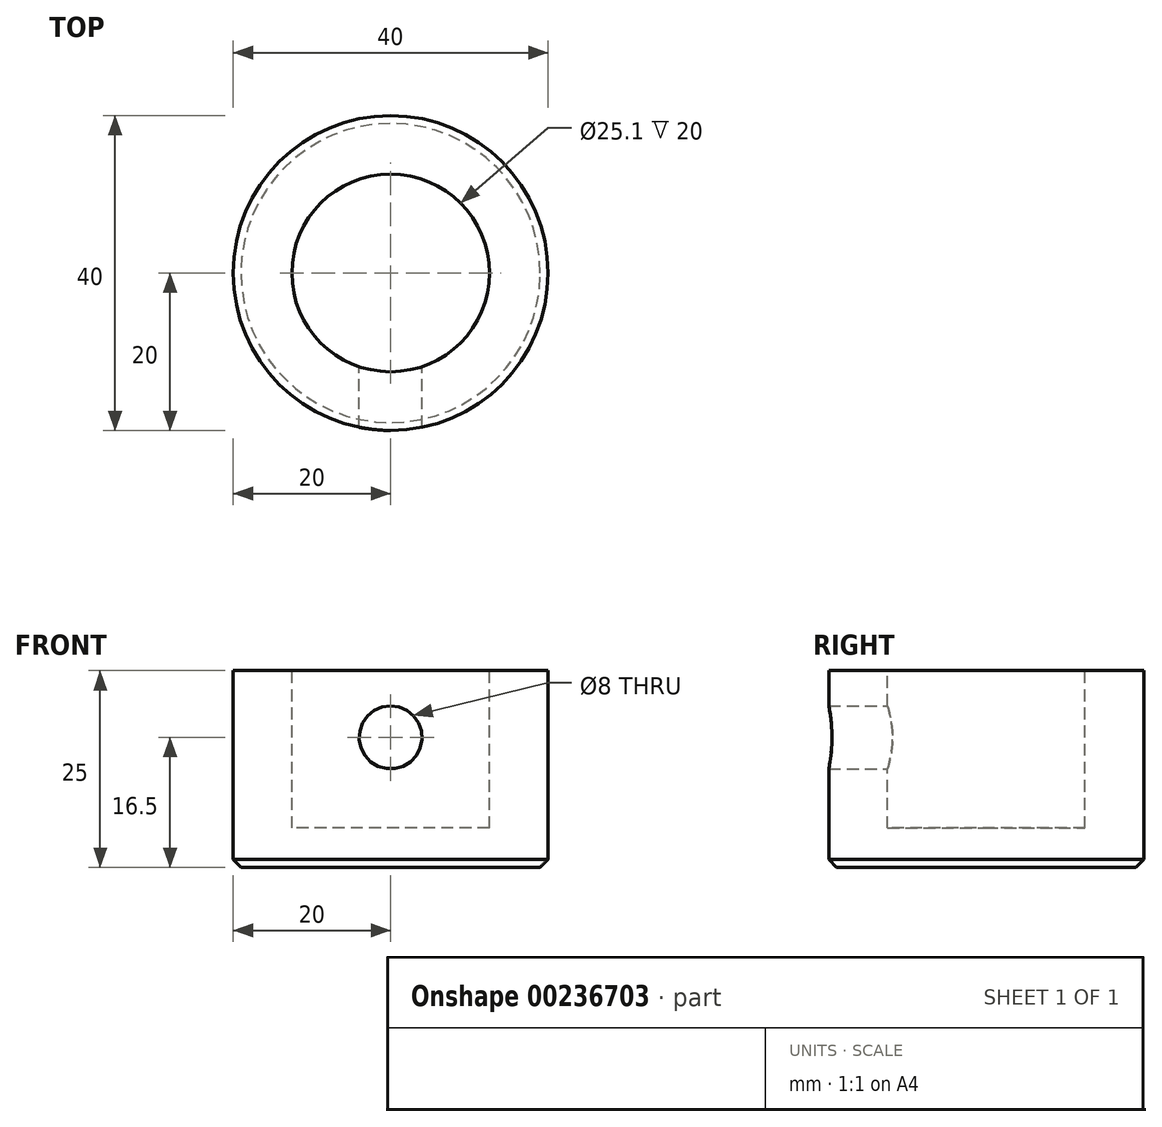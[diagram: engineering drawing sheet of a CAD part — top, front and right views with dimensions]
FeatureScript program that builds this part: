
annotation { "Feature Type Name" : "Feature", "Feature Type Description" : "" }
export const myFeature = defineFeature(function(context is Context, id is Id, definition is map)
    precondition{}
    {
        {
            var Q0;
            Q0=qCreatedBy(makeId("Top.planeOp"),FACE);
            var sketch = newSketch(context, id + "F0", { "sketchPlane" : qUnion([Q0])});
            skCircle(sketch, "E0", {"center": v(0, 0) * mm, "radius": 20 * mm});
            skSolve(sketch);
        }
        {
            var Q0;
            Q0=makeQuery(id+"F0.imprint","IMPRINT",FACE,{"disambiguationData":[TD([[makeQuery(id+"F0.imprint","IMPRINT",EDGE,{"derivedFrom":sQuery(id+"F0.wireOp",EDGE,"E0")}),1.0]])]});
            extrude(context, id + "F1", {"entities" : qUnion([Q0]), "depth" : 25 * mm, "offsetDistance" : 25 * mm});
        }
        {
            var Q0;
            Q0=makeQuery(id+"F1.opExtrude","CAP_FACE",FACE,{"disambiguationData":[OSD([sQuery(id+"F0.wireOp",EDGE,"E0")])],"isStart":false});
            var sketch = newSketch(context, id + "F2", { "sketchPlane" : qUnion([Q0])});
            skCircle(sketch, "E1", {"center": v(0, 0) * mm, "radius": 12.55 * mm});
            skSolve(sketch);
        }
        {
            var Q0;
            Q0 = qSketchRegion(id + "F2", true);
            extrude(context, id + "F3", {"entities" : qUnion([Q0]), "operationType" : NewBodyOperationType.REMOVE, "oppositeDirection" : true, "depth" : 20 * mm, "offsetDistance" : 25 * mm});
        }
        {
            var Q0;
            Q0=qCreatedBy(makeId("Front.planeOp"),FACE);
            var sketch = newSketch(context, id + "F4", { "sketchPlane" : qUnion([Q0])});
            skCircle(sketch, "E2", {"center": v(0, 16.5) * mm, "radius": 4 * mm});
            skSolve(sketch);
        }
        {
            var Q0;
            Q0 = qSketchRegion(id + "F4", true);
            extrude(context, id + "F5", {"entities" : qUnion([Q0]), "operationType" : NewBodyOperationType.REMOVE, "depth" : 25 * mm, "offsetDistance" : 25 * mm});
        }
        {
            var Q0;
            Q0=makeQuery(id+"F1.opExtrude","CAP_EDGE",EDGE,{"disambiguationData":[OSD([sQuery(id+"F0.wireOp",EDGE,"E0")])],"isStart":true});
            var Q1;
            Q1=makeQuery(id+"F3.boolean.opBoolean","COPY",EDGE,{"derivedFrom":makeQuery(id+"F3.opExtrude","CAP_EDGE",EDGE,{"disambiguationData":[OSD([sQuery(id+"F2.wireOp",EDGE,"E1")])],"isStart":true})});
            chamfer(context, id + "F6", {"entities" : qUnion([Q0, Q1]), "width" : 1 * mm, "tangentPropagation" : true});
        }
    });
